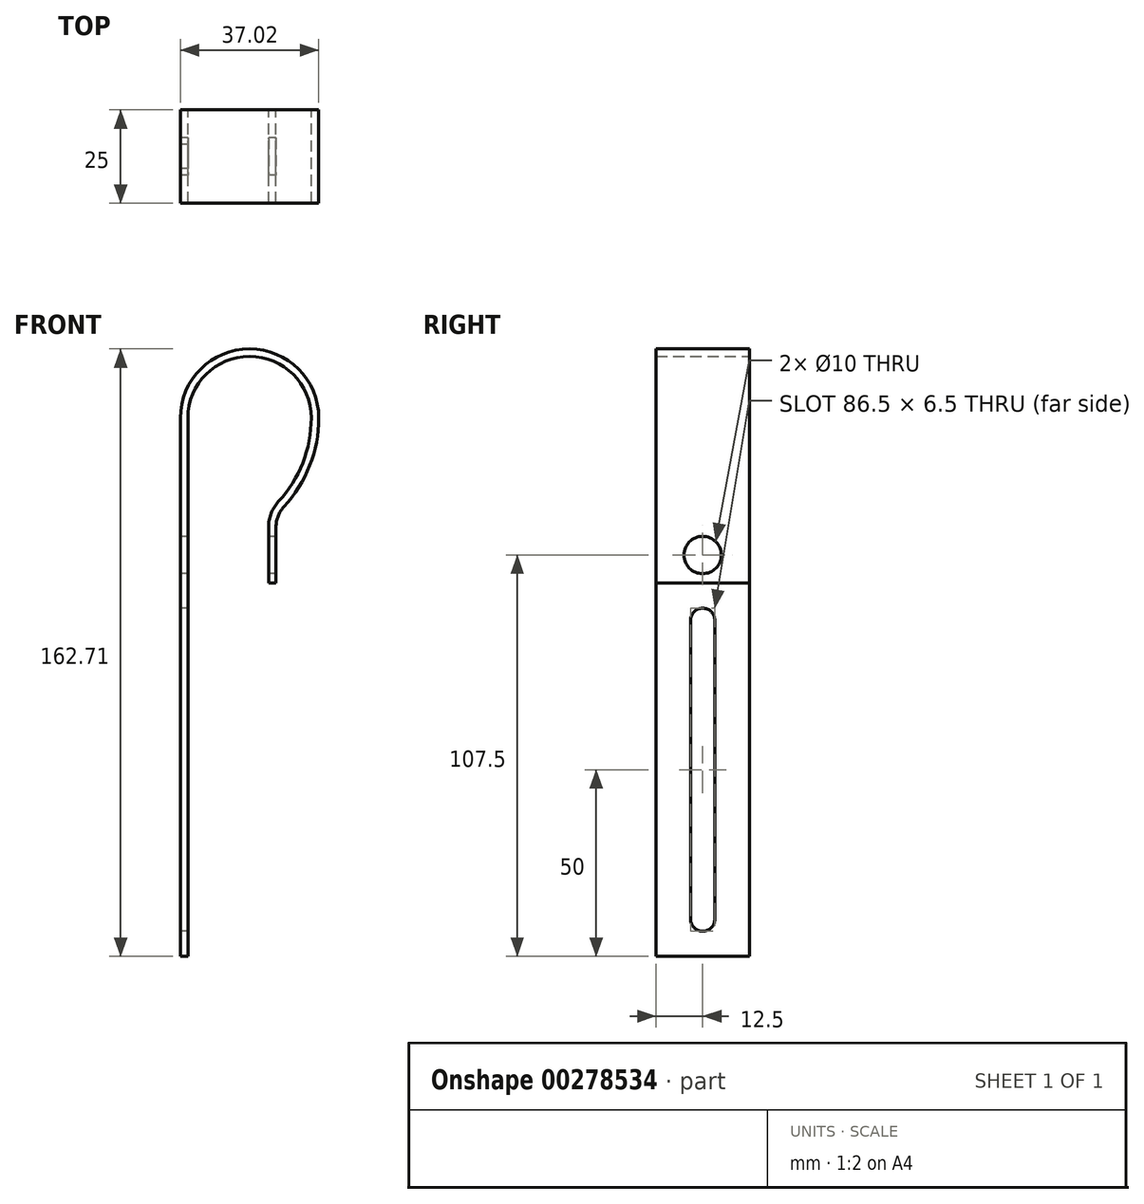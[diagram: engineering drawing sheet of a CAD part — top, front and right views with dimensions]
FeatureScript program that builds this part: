
annotation { "Feature Type Name" : "Feature", "Feature Type Description" : "" }
export const myFeature = defineFeature(function(context is Context, id is Id, definition is map)
    precondition{}
    {
        {
            var Q0;
            Q0=qCreatedBy(makeId("Front.planeOp"),FACE);
            var sketch = newSketch(context, id + "F0", { "sketchPlane" : qUnion([Q0])});
            skLineSegment(sketch, "E0", {"start": v(0, 0) * mm, "end": v(0, 144.2) * mm});
            skArc(sketch, "E1", {"start": v(33.02, 144.2) * mm, "mid": v(16.51, 160.71) * mm, "end": v(0, 144.2) * mm});
            skArc(sketch, "E2", {"start": v(24.25, 121.79) * mm, "mid": v(30.75, 132.17) * mm, "end": v(33.02, 144.2) * mm});
            skArc(sketch, "E3", {"start": v(24.25, 121.79) * mm, "mid": v(22.28, 118.64) * mm, "end": v(21.6, 115) * mm});
            skLineSegment(sketch, "E4", {"start": v(21.59, 115) * mm, "end": v(21.59, 100) * mm});
            skCircle(sketch, "E5", {"center": v(16.51, 144.2) * mm, "radius": 15.88 * mm, "construction": true});
            skLineSegment(sketch, "E6.0", {"start": v(23.6, 115) * mm, "end": v(23.6, 100) * mm});
            skLineSegment(sketch, "E6.1", {"start": v(-2, 0) * mm, "end": v(-2, 144.2) * mm});
            skArc(sketch, "E6.2", {"start": v(35.02, 144.2) * mm, "mid": v(16.51, 162.71) * mm, "end": v(-2, 144.2) * mm});
            skArc(sketch, "E6.3", {"start": v(25.72, 120.43) * mm, "mid": v(32.61, 131.44) * mm, "end": v(35.02, 144.2) * mm});
            skArc(sketch, "E6.4", {"start": v(25.72, 120.43) * mm, "mid": v(24.14, 117.92) * mm, "end": v(23.6, 115) * mm});
            skLineSegment(sketch, "E7", {"start": v(21.59, 100) * mm, "end": v(23.6, 100) * mm});
            skLineSegment(sketch, "E8", {"start": v(-2, 0) * mm, "end": v(0, 0) * mm});
            skSolve(sketch);
        }
        {
            var Q0;
            Q0=makeQuery(id+"F0.imprint","IMPRINT",FACE,{"disambiguationData":[TD([[makeQuery(id+"F0.imprint","IMPRINT",EDGE,{"derivedFrom":sQuery(id+"F0.wireOp",EDGE,"E0")}),1.0]])]});
            extrude(context, id + "F1", {"entities" : qUnion([Q0]), "depth" : 25 * mm});
        }
        {
            var Q0;
            Q0=makeQuery(id+"F1.opExtrude","SWEPT_FACE",FACE,{"disambiguationData":[OSD([sQuery(id+"F0.wireOp",EDGE,"E6.1")])]});
            var sketch = newSketch(context, id + "F2", { "sketchPlane" : qUnion([Q0])});
            skLineSegment(sketch, "E9", {"start": v(12.5, 0) * mm, "end": v(12.5, 144.2) * mm, "construction": true});
            skLineSegment(sketch, "E10.left", {"start": v(15.75, 10) * mm, "end": v(15.75, 90) * mm});
            skLineSegment(sketch, "E10.right", {"start": v(9.25, 10) * mm, "end": v(9.25, 90) * mm});
            skPoint(sketch, "E10.middle", {"position": v(12.5, 50) * mm});
            skArc(sketch, "E11", {"start": v(9.25, 10) * mm, "mid": v(12.5, 6.75) * mm, "end": v(15.75, 10) * mm});
            skArc(sketch, "E12", {"start": v(15.75, 90) * mm, "mid": v(12.5, 93.25) * mm, "end": v(9.25, 90) * mm});
            skCircle(sketch, "E13", {"center": v(12.5, 107.5) * mm, "radius": 5 * mm});
            skSolve(sketch);
        }
        {
            var Q0;
            Q0 = qSketchRegion(id + "F2", true);
            extrude(context, id + "F3", {"entities" : qUnion([Q0]), "operationType" : NewBodyOperationType.REMOVE, "endBound" : BoundingType.THROUGH_ALL, "oppositeDirection" : true, "depth" : 25 * mm});
        }
    });
